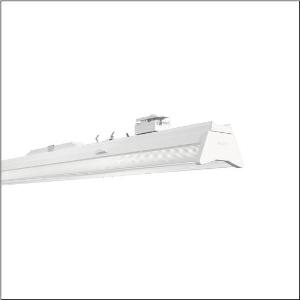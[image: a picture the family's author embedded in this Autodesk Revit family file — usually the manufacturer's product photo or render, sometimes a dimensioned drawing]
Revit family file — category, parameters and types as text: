
# Revit family: licross_11_performance_ho_51tm16mn4gxm
name_source: partatom
category: Lighting Fixtures
units: mm (PartAtom-declared; Revit-internal decimal feet)

## family parameters
Cut with Voids When Loaded = No
Host = Face
Light Source = No
Part Type = Normal
Room Calculation Point = No
Round Connector Dimension = Use Diameter
Shared = No

## types (1)
- --- (1 x LED, 16020 lm, 87.4 W, 4000K)
    Apparent Load = 87 VA
    CIE Flux Codes = 63 87 95 78 100
    Color Rendering = 80
    Color Temperature = 4000K
    Default Elevation = 1800 mm
    Description = Licross 11 Performance HO, luminaire insert, of sheet steel, galvanised, coil coated, white, length: 1.500mm, width: 120mm, height: 123mm, LED rated luminous flux: 16.020lm, light colour: 840, SDCM (Standard Deviation of Colour Matching)MacAdam ≤ 2 SDCM (initial), control gear: ON/OFF Multilumen, with plug, 3-pole, with phase selection, mains connection: 220..240V, AC, 50/60Hz, rated input power: 87W, internal wiring halogen-free, primary light control with lens, of plastic, primary optical cover: cover, of PMMA, light emission: direct/indirect distribution, primary light characteristic: symmetric, protection rating (complete): IP40, insulation class (complete): insulation class I (protective earthing), certification: CE, ENEC, VDE, UKCA, protection symbol: D if used in an environment without relevant dust loads with corresponding accessories, impact resistance: IK06, permissible ambient temperature for indoor applications: -35..+35°C, corresponds to IFS (International Featured Standards) requirements for safety and quality in the food industry, reducing of maximum allowable ambient temperature of 5°C with ceiling mounting, LABS conformity tested according to VDMA 24364:2018-05, The light source and the operating device comply with the requirements of the Ecodesign Regulation (EU) 2019/2020 and are replaceable in accordance with this regulation, packaging unit: 1 piece
    Height = 114 mm
    Lamp = 1 x LED
    Lamp Light Flux = 16020 lm
    Lamp Power = 87.4 W
    Lamp count = 1
    Length = 1500 mm
    Luminous efficacy = 183 lm/W
    Manufacturer = Siteco
    ModVariant = No
    Model = 51TM16MN4GXM
    Mounting Place = Ceiling
    Mounting Type = Pendant
    Number of Poles = 1
    OnlyDefault = Yes
    Power Factor = 1
    Product Name = Licross 11 Performance HO
    Product group = luminaire insert | ceiling pendant
    ProductGroupID = 901
    Protection Class = Protection class I
    Protection Degree = IP 40
    RLX_Detail_Level = 1
    RLX_Emergency_Light_Flux = 0 lm
    RLX_Emergency_Type = 0
    RLX_Emergency_Type_DB = No
    RlxData = <blob elided: 32077 chars, md5=2ed32f98>
    Socket = socket
    Standby Power = 0 W
    System Light Flux = 16020 lm
    System Power = 87 W
    Type Comments = factory setting: luminous flux: 100 % | (A | C | E) | 203 mA
    Type Image = l_1256138.jpg
    URL = http://relux.com
    VarID = @adj_092163
    Voltage = 0 V
    Weight = 0.00 kg
    Width = 120 mm

## geometry (parser evidence)
native form markers: Blend x4, Sweep x13
no freeform markers — native parametric forms only
